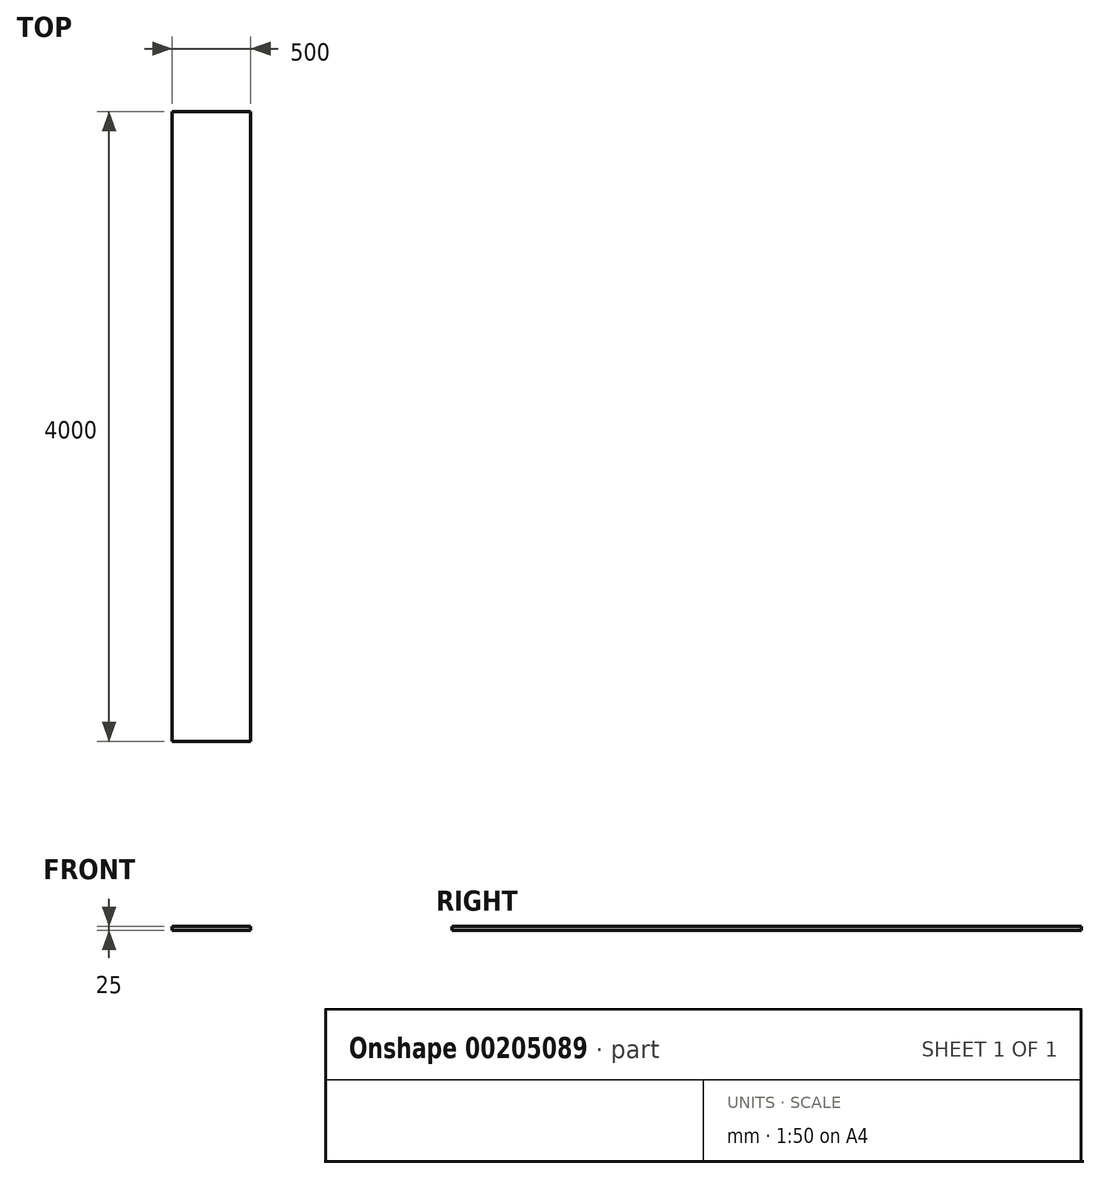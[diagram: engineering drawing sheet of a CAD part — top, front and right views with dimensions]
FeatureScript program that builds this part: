
annotation { "Feature Type Name" : "Feature", "Feature Type Description" : "" }
export const myFeature = defineFeature(function(context is Context, id is Id, definition is map)
    precondition{}
    {
        {
            var Q0;
            Q0=qCreatedBy(makeId("Top.planeOp"),FACE);
            var sketch = newSketch(context, id + "F0", { "sketchPlane" : qUnion([Q0])});
            skLineSegment(sketch, "E0.bottom", {"start": v(250, 2000) * mm, "end": v(-250, 2000) * mm});
            skLineSegment(sketch, "E0.top", {"start": v(250, -2000) * mm, "end": v(-250, -2000) * mm});
            skLineSegment(sketch, "E0.left", {"start": v(250, 2000) * mm, "end": v(250, -2000) * mm});
            skLineSegment(sketch, "E0.right", {"start": v(-250, 2000) * mm, "end": v(-250, -2000) * mm});
            skPoint(sketch, "E0.middle", {"position": v(0, 0) * mm});
            skSolve(sketch);
        }
        {
            var Q0;
            Q0 = qSketchRegion(id + "F0", true);
            extrude(context, id + "F1", {"entities" : qUnion([Q0]), "oppositeDirection" : true, "depth" : 25 * mm});
        }
    });
